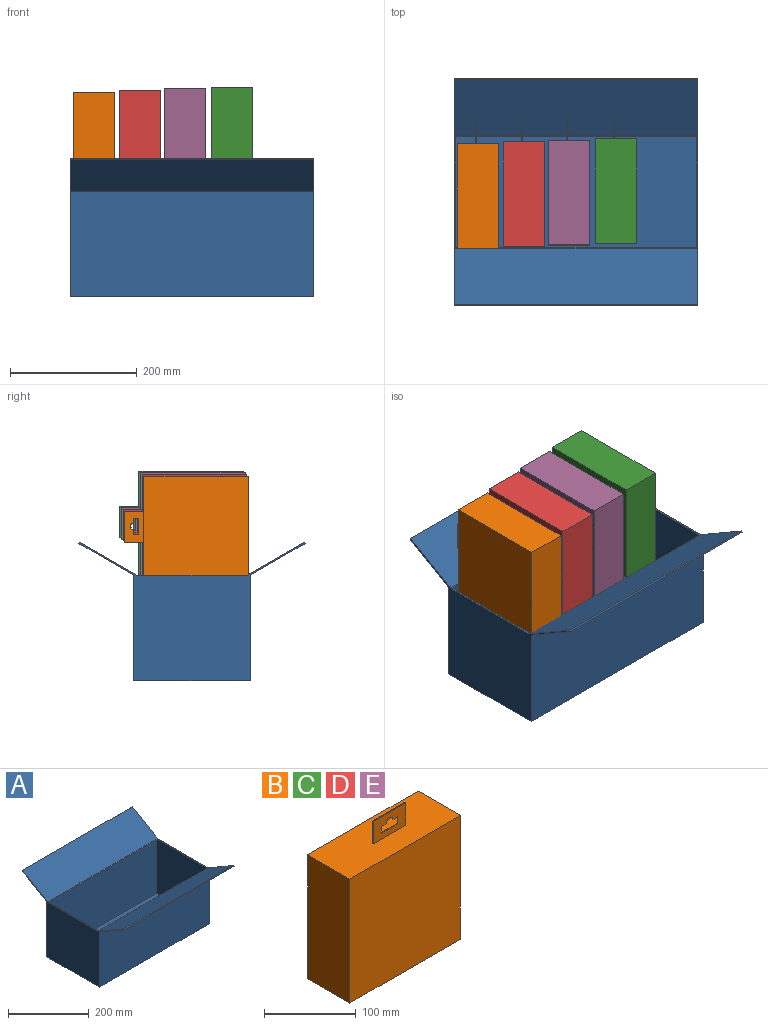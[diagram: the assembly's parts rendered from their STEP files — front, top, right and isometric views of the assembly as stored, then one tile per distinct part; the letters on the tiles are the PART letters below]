
ASSEMBLY  parts=5 mates=4
PART A: 20 faces, bbox 384x357.3x219.1 mm
  f0: plane 173.99x2.5mm, normal (0,0,1), area 435mm2, adj f2,f7,f14,f19
  f1: plane 173.99x2.5mm, normal (0,0,1), area 435mm2, adj f4,f9,f14,f19
  f2: plane 357.26x219.12mm, normal (-1,0,0), area 31238.8mm2, adj f0,f3,f5,f6,f12,f14,f15,f16
  f3: plane 384x167mm, normal (0,-1,0), area 64128mm2, adj f2,f4,f6,f12
  f4: plane 357.26x219.12mm, normal (1,0,0), area 31238.8mm2, adj f1,f3,f5,f6,f12,f14,f15,f16
  f5: plane 384x167mm, normal (0,1,0), area 64128mm2, adj f2,f4,f6,f16
  f6: plane 384x184mm, normal (0,0,-1), area 70656mm2, adj f2,f3,f4,f5
  f7: plane 179x164.5mm, normal (1,0,0), area 29445.5mm2, adj f0,f8,f10,f11,f13,f17
  f8: plane 379x164.5mm, normal (0,1,0), area 62345.5mm2, adj f7,f9,f11,f13
  f9: plane 179x164.5mm, normal (-1,0,0), area 29445.5mm2, adj f1,f8,f10,f11,f13,f17
  f10: plane 379x164.5mm, normal (0,-1,0), area 62345.5mm2, adj f7,f9,f11,f17
  f11: plane 379x179mm, normal (0,0,1), area 67841mm2, adj f7,f8,f9,f10
  f12: plane 384x86.63mm, normal (0,-0.5,-0.87), area 38400mm2, adj f2,f3,f4,f15
  f13: plane 379x2.51mm, normal (0,0,-1), area 949.3mm2, adj f7,f8,f9,f14
  f14: plane 384x90.39mm, normal (0,0.5,0.87), area 40064.9mm2, adj f0,f1,f2,f4,f13,f15
  f15: plane 384x2.17mm, normal (0,-0.87,0.5), area 960mm2, adj f2,f4,f12,f14
  f16: plane 384x86.63mm, normal (0,0.5,-0.87), area 38400mm2, adj f2,f4,f5,f18
  f17: plane 379x2.51mm, normal (0,0,-1), area 949.3mm2, adj f7,f9,f10,f19
  f18: plane 384x2.17mm, normal (0,0.87,0.5), area 960mm2, adj f2,f4,f16,f19
  f19: plane 384x90.39mm, normal (0,-0.5,0.87), area 40064.9mm2, adj f0,f1,f2,f4,f17,f18
PART B: 17 faces, bbox 170x65x195 mm
  f0: plane 165x65mm, normal (-1,0,0), area 10725mm2, adj f1,f3,f4,f5
  f1: plane 170x65mm, normal (0,0,-1), area 11050mm2, adj f0,f2,f4,f5
  f2: plane 165x65mm, normal (1,0,0), area 10725mm2, adj f1,f3,f4,f5
  f3: plane 170x65mm, normal (0,0,1), area 10998.3mm2, adj f0,f2,f4,f5,f6,f7,f8,f9
  f4: plane 170x165mm, normal (0,-1,0), area 28050mm2, adj f0,f1,f2,f3
  f5: plane 170x165mm, normal (0,1,0), area 28050mm2, adj f0,f1,f2,f3
  f6: plane 30x1.03mm, normal (-1,0,0), area 31mm2, adj f3,f7,f9,f10
  f7: plane 50x30mm, normal (0,-1,0), area 1232.6mm2, adj f3,f6,f8,f10,f11,f12,f13,f14
  f8: plane 30x1.03mm, normal (1,0,0), area 31mm2, adj f3,f7,f9,f10
  f9: plane 50x30mm, normal (0,1,0), area 1232.6mm2, adj f3,f6,f8,f10,f11,f12,f13,f14
  f10: plane 50x1.03mm, normal (0,0,1), area 51.7mm2, adj f6,f7,f8,f9
  f11: plane 7.57x1.03mm, normal (0,0,-1), area 7.8mm2, adj f7,f9,f12,f16
  f12: plane 8.98x1.03mm, normal (-1,0,0), area 9.3mm2, adj f7,f9,f11,f13
  f13: plane 25.28x1.03mm, normal (0,0,1), area 26.1mm2, adj f7,f9,f12,f14
  f14: plane 8.98x1.03mm, normal (1,0,0), area 9.3mm2, adj f7,f9,f13,f15
  f15: plane 7.57x1.03mm, normal (0,0,-1), area 7.8mm2, adj f7,f9,f14,f16
  f16: cylinder r=5.07mm len=10.14mm, axis (0,1,0), area 16.5mm2, adj f7,f9,f11,f15
PART C: same geometry as B
PART D: same geometry as B
PART E: same geometry as B
PLACE A t=(-69.81,-1.84,-54.08)mm
PLACE B rot(axis=(-0.58,-0.58,-0.58),120deg) t=(-0.24,1.1,99.06)mm
PLACE C rot(axis=(-0.58,-0.58,-0.58),120deg) t=(217.86,8.86,106.97)mm
PLACE D rot(axis=(-0.58,-0.58,-0.58),120deg) t=(72.03,4.05,102.05)mm
PLACE E rot(axis=(-0.58,-0.58,-0.58),120deg) t=(143.57,6.29,105.04)mm
MATE parallel D.f3 <-> A.f5  axis (0,1,0) through (39.55,169.05,187.02)mm
MATE parallel B.f1 <-> A.f8  axis (0,-1,0) through (-32.74,1.1,184.06)mm
MATE parallel E.f3 <-> A.f5  axis (0,1,0) through (111.09,171.29,190.01)mm
MATE parallel C.f3 <-> A.f5  axis (0,1,0) through (185.37,173.86,191.95)mm
